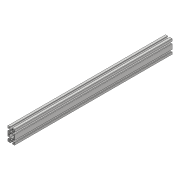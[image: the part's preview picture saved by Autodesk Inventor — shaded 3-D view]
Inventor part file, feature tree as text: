
AUTODESK INVENTOR PART (.ipt)
format: ipt  version: 2018 (Build 220112000, 112)  size: 241,152 bytes
history: native  units: mm
features: extrude x1, sketch x1
ambient origin geometry x8: Origin, YZ Plane, XZ Plane, XY Plane, X Axis, Y Axis, Z Axis, Center Point
bodies: Solid1 (feature_tree)
feature tree (2):
  extrude  "Extrusion1"  [1 undecoded]
  sketch  "Sketch1"  dims[d0=450.0mm d1=0.0mm]
note: 1 required parameter value undecoded (feature->parameter linkage not recoverable at this tier; creation-order binding heuristic only, values carry confidence <= 0.55)
